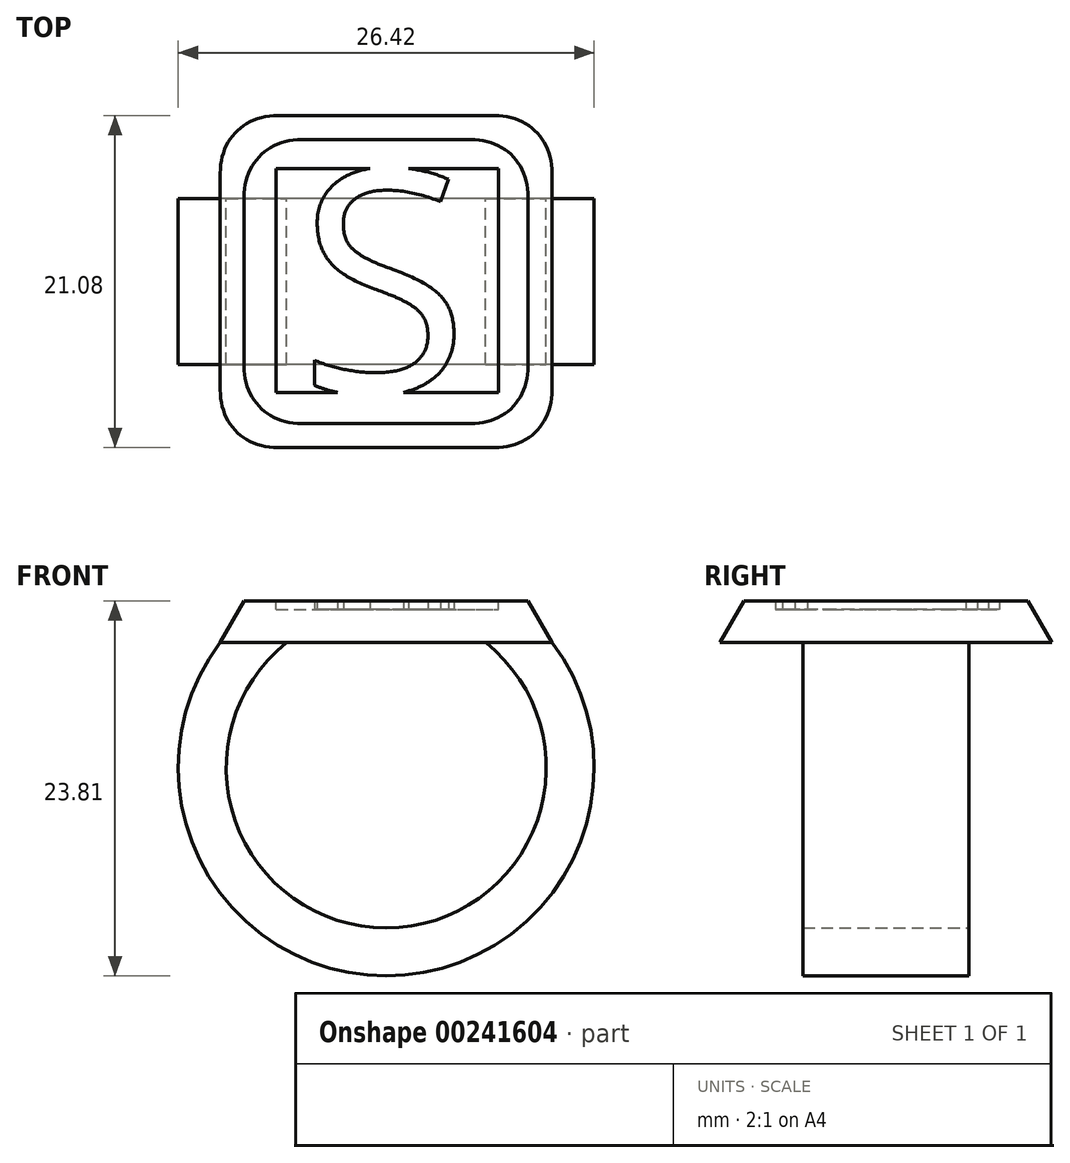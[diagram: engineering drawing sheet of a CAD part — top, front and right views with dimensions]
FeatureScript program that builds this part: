
annotation { "Feature Type Name" : "Feature", "Feature Type Description" : "" }
export const myFeature = defineFeature(function(context is Context, id is Id, definition is map)
    precondition{}
    {
        {
            var Q0;
            Q0=qCreatedBy(makeId("Top.planeOp"),FACE);
            var sketch = newSketch(context, id + "F0", { "sketchPlane" : qUnion([Q0])});
            skLineSegment(sketch, "E0.bottom", {"start": v(-12.7, 12.7) * mm, "end": v(12.7, 12.7) * mm});
            skLineSegment(sketch, "E0.top", {"start": v(-12.7, -12.7) * mm, "end": v(12.7, -12.7) * mm});
            skLineSegment(sketch, "E0.left", {"start": v(-12.7, 12.7) * mm, "end": v(-12.7, -12.7) * mm});
            skLineSegment(sketch, "E0.right", {"start": v(12.7, 12.7) * mm, "end": v(12.7, -12.7) * mm});
            skPoint(sketch, "E0.middle", {"position": v(0, 0) * mm});
            skSolve(sketch);
        }
        {
            var Q0;
            Q0 = qSketchRegion(id + "FitRWTINHqRWTHi_0", true);
            var Q1;
            Q1=makeQuery(id+"F0.imprint","IMPRINT",FACE,{"disambiguationData":[TD([[makeQuery(id+"F0.imprint","IMPRINT",EDGE,{"derivedFrom":sQuery(id+"F0.wireOp",EDGE,"E0.bottom")}),-1.0]])]});
            extrude(context, id + "F1", {"entities" : qUnion([Q0, Q1]), "depth" : 3.17 * mm, "hasDraft" : true, "draftAngle" : 30 * degree, "draftPullDirection" : true});
        }
        {
            var Q0;
            Q0=qCreatedBy(makeId("Front.planeOp"),FACE);
            var sketch = newSketch(context, id + "F2", { "sketchPlane" : qUnion([Q0])});
            skArc(sketch, "E1", {"start": v(-10.16, 0) * mm, "mid": v(0, -23.56) * mm, "end": v(10.16, 0) * mm});
            skSolve(sketch);
        }
        {
            var Q0;
            Q0=makeQuery(id+"F1.opExtrude","CAP_FACE",FACE,{"disambiguationData":[OSD([sQuery(id+"F0.wireOp",EDGE,"E0.bottom"),sQuery(id+"F0.wireOp",EDGE,"E0.top"),sQuery(id+"F0.wireOp",EDGE,"E0.left"),sQuery(id+"F0.wireOp",EDGE,"E0.right")])],"isStart":true});
            var sketch = newSketch(context, id + "F3", { "sketchPlane" : qUnion([Q0])});
            skLineSegment(sketch, "E2.bottom", {"start": v(12.7, 6.35) * mm, "end": v(7.62, 6.35) * mm});
            skLineSegment(sketch, "E2.top", {"start": v(12.7, -6.35) * mm, "end": v(7.62, -6.35) * mm});
            skLineSegment(sketch, "E2.left", {"start": v(12.7, 6.35) * mm, "end": v(12.7, -6.35) * mm});
            skLineSegment(sketch, "E2.right", {"start": v(7.62, 6.35) * mm, "end": v(7.62, -6.35) * mm});
            skPoint(sketch, "E2.middle", {"position": v(10.16, 0) * mm});
            skSolve(sketch);
        }
        {
            var Q0;
            Q0 = qSketchRegion(id + "F3", true);
            var Q1;
            Q1 = qConstructionFilter(qBodyType(qCreatedBy(id + "F2" ,EDGE), BodyType.WIRE), ConstructionObject.NO);
            sweep(context, id + "F4", {"operationType" : NewBodyOperationType.ADD, "profiles" : qUnion([Q0]), "path" : qUnion([Q1])});
        }
        {
            var Q0;
            Q0=qCreatedBy(makeId("Front.planeOp"),FACE);
            var sketch = newSketch(context, id + "F5", { "sketchPlane" : qUnion([Q0])});
            skLineSegment(sketch, "E3.0", {"start": v(-10.16, 0) * mm, "end": v(-10.01, -2.54) * mm});
            skLineSegment(sketch, "E4.0.0", {"start": v(7.62, 0) * mm, "end": v(12.7, 0) * mm});
            skLineSegment(sketch, "E4.0.2", {"start": v(7.62, 0) * mm, "end": v(12.7, 0) * mm});
            skLineSegment(sketch, "E4.0.4", {"start": v(-12.7, 0) * mm, "end": v(12.7, 0) * mm});
            skLineSegment(sketch, "E4.0.6", {"start": v(-12.7, 0) * mm, "end": v(-10.16, 0) * mm});
            skLineSegment(sketch, "E4.0.8", {"start": v(-10.16, 0) * mm, "end": v(-12.7, 0) * mm});
            skLineSegment(sketch, "E4.0.10", {"start": v(-12.7, 0) * mm, "end": v(12.7, 0) * mm});
            skArc(sketch, "E5", {"start": v(-2.1, 2.48) * mm, "mid": v(-6.56, 0.76) * mm, "end": v(-10.01, -2.54) * mm});
            skSolve(sketch);
        }
        {
            var Q0;
            Q0=qCreatedBy(makeId("Front.planeOp"),FACE);
            var sketch = newSketch(context, id + "F6", { "sketchPlane" : qUnion([Q0])});
            skLineSegment(sketch, "E6.0", {"start": v(-10.16, 0) * mm, "end": v(-10.01, -2.54) * mm});
            skLineSegment(sketch, "E7.0", {"start": v(-12.7, 0) * mm, "end": v(12.7, 0) * mm});
            skArc(sketch, "E8", {"start": v(-7.62, 0) * mm, "mid": v(-8.9, -1.18) * mm, "end": v(-10.01, -2.54) * mm});
            skSolve(sketch);
        }
        {
            var Q0;
            {var subQ0=sQuery(id+"F6.wireOp",EDGE,"E6.0");Q0=makeQuery(id+"F6.imprint","IMPRINT",FACE,{"disambiguationData":[TD([[makeQuery(id+"F6.imprint","IMPRINT",EDGE,{"derivedFrom":subQ0}),1.0]])]});}
            extrude(context, id + "F7", {"entities" : qUnion([Q0]), "operationType" : NewBodyOperationType.ADD, "endBound" : BoundingType.SYMMETRIC, "depth" : 12.7 * mm});
        }
        {
            var Q0;
            Q0=makeQuery(id+"F1.opExtrude","SWEPT_EDGE",EDGE,{"disambiguationData":[OSD([sQuery(id+"F0.wireOp",EDGE,"E0.bottom"),sQuery(id+"F0.wireOp",EDGE,"E0.left")])]});
            var Q1;
            Q1=makeQuery(id+"F1.opExtrude","SWEPT_EDGE",EDGE,{"disambiguationData":[OSD([sQuery(id+"F0.wireOp",EDGE,"E0.bottom"),sQuery(id+"F0.wireOp",EDGE,"E0.right")])]});
            var Q2;
            Q2=makeQuery(id+"F1.opExtrude","SWEPT_EDGE",EDGE,{"disambiguationData":[OSD([sQuery(id+"F0.wireOp",EDGE,"E0.top"),sQuery(id+"F0.wireOp",EDGE,"E0.right")])]});
            var Q3;
            Q3=makeQuery(id+"F1.opExtrude","SWEPT_EDGE",EDGE,{"disambiguationData":[OSD([sQuery(id+"F0.wireOp",EDGE,"E0.top"),sQuery(id+"F0.wireOp",EDGE,"E0.left")])]});
            fillet(context, id + "F8", {"entities" : qUnion([Q0, Q1, Q2, Q3]), "radius" : 5.08 * mm, "tangentPropagation" : true, "allowEdgeOverflow" : false});
        }
        {
            var Q0;
            Q0=makeQuery(id+"F1.opExtrude","CAP_FACE",FACE,{"disambiguationData":[OSD([sQuery(id+"F0.wireOp",EDGE,"E0.bottom"),sQuery(id+"F0.wireOp",EDGE,"E0.top"),sQuery(id+"F0.wireOp",EDGE,"E0.left"),sQuery(id+"F0.wireOp",EDGE,"E0.right")])],"isStart":false});
            var sketch = newSketch(context, id + "F9", { "sketchPlane" : qUnion([Q0])});
            skLineSegment(sketch, "E9.bottom", {"start": v(-8.43, 8.66) * mm, "end": v(8.59, 8.66) * mm});
            skLineSegment(sketch, "E9.top", {"start": v(-8.43, -8.47) * mm, "end": v(8.59, -8.47) * mm});
            skLineSegment(sketch, "E9.left", {"start": v(-8.43, 8.66) * mm, "end": v(-8.43, -8.47) * mm});
            skLineSegment(sketch, "E9.right", {"start": v(8.59, 8.66) * mm, "end": v(8.59, -8.47) * mm});
            skSolve(sketch);
        }
        {
            var Q0;
            Q0=makeQuery(id+"F9.imprint","IMPRINT",FACE,{"disambiguationData":[TD([[makeQuery(id+"F9.imprint","IMPRINT",EDGE,{"derivedFrom":sQuery(id+"F9.wireOp",EDGE,"E9.bottom")}),-1.0]])]});
            extrude(context, id + "F10", {"entities" : qUnion([Q0]), "operationType" : NewBodyOperationType.REMOVE, "endBound" : BoundingType.SYMMETRIC, "oppositeDirection" : true, "depth" : 1.27 * mm});
        }
        {
            var Q0;
            Q0=makeQuery(id+"F10.boolean.opBoolean","COPY",FACE,{"derivedFrom":makeQuery(id+"F10.opExtrude","CAP_FACE",FACE,{"disambiguationData":[OSD([sQuery(id+"F9.wireOp",EDGE,"E9.bottom"),sQuery(id+"F9.wireOp",EDGE,"E9.top"),sQuery(id+"F9.wireOp",EDGE,"E9.left"),sQuery(id+"F9.wireOp",EDGE,"E9.right")])],"isStart":false})});
            var sketch = newSketch(context, id + "F11", { "sketchPlane" : qUnion([Q0])});
            skText(sketch, "E10", { "text": "S", "fontName": "OpenSans-Regular.ttf"});
            const initialGuessF11  = {"E10": [-0.00673, -0.00847, 1, 0, 0.01713]};
            skSetInitialGuess(sketch, initialGuessF11);
            skSolve(sketch);
        }
        {
            var Q0;
            Q0 = qSketchRegion(id + "F11", true);
            extrude(context, id + "F12", {"entities" : qUnion([Q0]), "operationType" : NewBodyOperationType.ADD, "depth" : 0.64 * mm});
        }
        {
            var Q0;
            Q0=makeQuery(id+"F1.opExtrude","SWEPT_BODY",BODY,{"disambiguationData":[OSD([sQuery(id+"F0.wireOp",EDGE,"E0.bottom"),sQuery(id+"F0.wireOp",EDGE,"E0.top"),sQuery(id+"F0.wireOp",EDGE,"E0.left"),sQuery(id+"F0.wireOp",EDGE,"E0.right")])]});
            var Q1;
            Q1=qCreatedBy(makeId("Origin.pointOp"),VERTEX);
            transform(context, id + "F13", {"entities" : qUnion([Q0]), "transformType" : TransformType.SCALE_UNIFORMLY, "scale" : .83, "scalePoint" : qUnion([Q1]), "makeCopy" : false});
        }
    });
